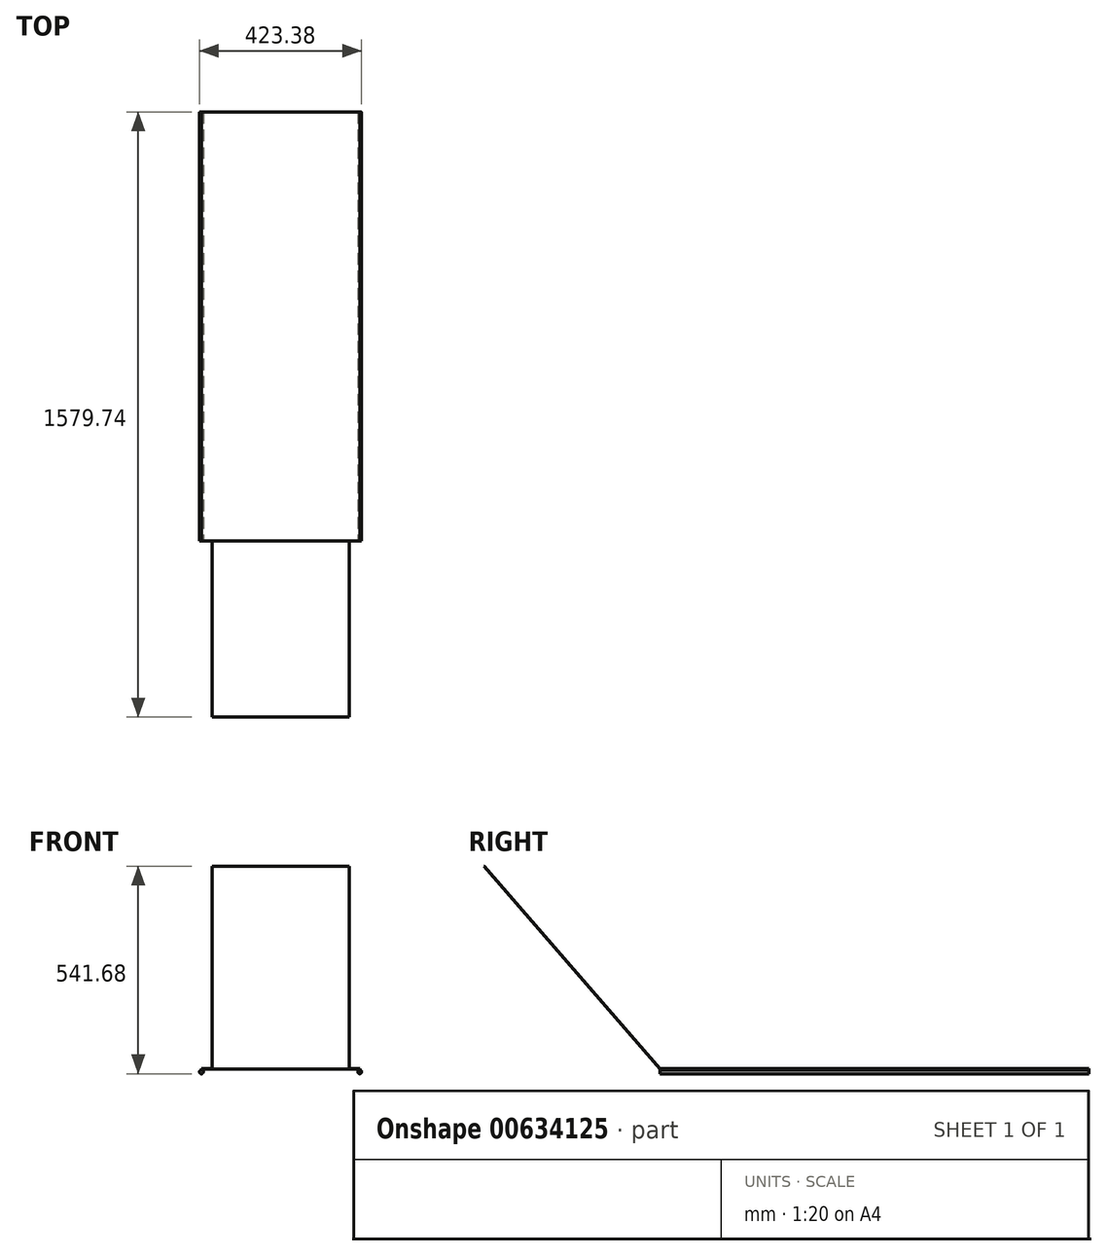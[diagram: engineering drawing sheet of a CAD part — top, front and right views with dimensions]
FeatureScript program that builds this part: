
annotation { "Feature Type Name" : "Feature", "Feature Type Description" : "" }
export const myFeature = defineFeature(function(context is Context, id is Id, definition is map)
    precondition{}
    {
        {
            var Q0;
            Q0=qCreatedBy(makeId("Front.planeOp"),FACE);
            var sketch = newSketch(context, id + "F0", { "sketchPlane" : qUnion([Q0])});
            skLineSegment(sketch, "E0.bottom", {"start": v(-15, 40) * mm, "end": v(15, 40) * mm});
            skLineSegment(sketch, "E0.top", {"start": v(-12, 0) * mm, "end": v(12, 0) * mm});
            skLineSegment(sketch, "E0.left", {"start": v(-15, 40) * mm, "end": v(-15, 37) * mm});
            skLineSegment(sketch, "E0.right", {"start": v(15, 37) * mm, "end": v(15, 3) * mm});
            skLineSegment(sketch, "E1.0", {"start": v(-15, 37) * mm, "end": v(3, 37) * mm});
            skLineSegment(sketch, "E1.1", {"start": v(-12, 6) * mm, "end": v(-12, 6) * mm});
            skLineSegment(sketch, "E1.2", {"start": v(-9, 3) * mm, "end": v(9, 3) * mm});
            skLineSegment(sketch, "E1.3", {"start": v(12, 29.6) * mm, "end": v(12, 6) * mm});
            skLineSegment(sketch, "E2.0", {"start": v(-15, 6) * mm, "end": v(-12, 6) * mm});
            skLineSegment(sketch, "E3", {"start": v(12, 40) * mm, "end": v(7.5, 40) * mm, "construction": true});
            skLineSegment(sketch, "E4", {"start": v(7, 34.8) * mm, "end": v(7, 40) * mm, "construction": true});
            skArc(sketch, "E5", {"start": v(7, 40) * mm, "mid": v(6.75, 29.6) * mm, "end": v(7.5, 39.98) * mm});
            skLineSegment(sketch, "E6.trimOffspring", {"start": v(-15, 6) * mm, "end": v(-15, 3) * mm});
            skPoint(sketch, "E7.orphan", {"position": v(5, 29.7) * mm});
            skPoint(sketch, "E8.visualSharp", {"position": v(15, 40) * mm});
            skArc(sketch, "E8.filletArc", {"start": v(15, 37) * mm, "mid": v(14.12, 39.12) * mm, "end": v(12, 40) * mm});
            skPoint(sketch, "E9.visualSharp", {"position": v(15, 0) * mm});
            skArc(sketch, "E9.filletArc", {"start": v(12, 0) * mm, "mid": v(14.12, 0.88) * mm, "end": v(15, 3) * mm});
            skArc(sketch, "E10.filletArc", {"start": v(9, 3) * mm, "mid": v(11.12, 3.88) * mm, "end": v(12, 6) * mm});
            skPoint(sketch, "E11.visualSharp", {"position": v(-12, 3) * mm});
            skArc(sketch, "E11.filletArc", {"start": v(-12, 6) * mm, "mid": v(-11.12, 3.88) * mm, "end": v(-9, 3) * mm});
            skPoint(sketch, "E12.visualSharp", {"position": v(-15, 0) * mm});
            skArc(sketch, "E12.filletArc", {"start": v(-15, 3) * mm, "mid": v(-14.12, 0.88) * mm, "end": v(-12, 0) * mm});
            skLineSegment(sketch, "E13.0", {"start": v(6.5, 34.8) * mm, "end": v(6.5, 39.8) * mm});
            skLineSegment(sketch, "E14.0", {"start": v(7.5, 34.8) * mm, "end": v(7.5, 40) * mm});
            skLineSegment(sketch, "E15", {"start": v(-15, 6) * mm, "end": v(-15, 16) * mm});
            skLineSegment(sketch, "E16", {"start": v(-15, 16) * mm, "end": v(-12, 16) * mm});
            skLineSegment(sketch, "E17", {"start": v(-12, 16) * mm, "end": v(-12, 6) * mm});
            skLineSegment(sketch, "E18", {"start": v(6.75, 29.6) * mm, "end": v(12, 29.6) * mm});
            skSolve(sketch);
        }
        {
            var Q0;
            Q0=qCreatedBy(makeId("Front.planeOp"),FACE);
            var sketch = newSketch(context, id + "F1", { "sketchPlane" : qUnion([Q0])});
            skLineSegment(sketch, "E19.1.1", {"start": v(7.5, 40) * mm, "end": v(-15, 40) * mm});
            skLineSegment(sketch, "E19.1.2", {"start": v(-15, 40) * mm, "end": v(-15, 37) * mm});
            skArc(sketch, "E19.2.8", {"start": v(-15, 3) * mm, "mid": v(-14.12, 0.88) * mm, "end": v(-12, 0) * mm, "construction": true});
            skLineSegment(sketch, "E19.2.9", {"start": v(-12, 0) * mm, "end": v(-5, 0) * mm});
            skLineSegment(sketch, "E19.2.13", {"start": v(17, 40) * mm, "end": v(8.5, 40) * mm});
            skLineSegment(sketch, "E19.3.0", {"start": v(-15, 18) * mm, "end": v(-15, 7.7) * mm});
            skPoint(sketch, "E20.2", {"position": v(6.5, 37.3) * mm});
            skPoint(sketch, "E21.orphan", {"position": v(6.5, 39.8) * mm});
            skPoint(sketch, "E19.0.2.end.orphan", {"position": v(7, 40) * mm});
            skPoint(sketch, "E22.orphan", {"position": v(12, 29.6) * mm});
            skPoint(sketch, "E23.orphan", {"position": v(7.5, 34.8) * mm});
            skPoint(sketch, "E20.0.start.orphan", {"position": v(6.5, 34.8) * mm});
            skLineSegment(sketch, "E24", {"start": v(-15, 37) * mm, "end": v(-15, 31) * mm});
            skLineSegment(sketch, "E25", {"start": v(0, 0) * mm, "end": v(0, 15) * mm, "construction": true});
            skLineSegment(sketch, "E26", {"start": v(7.5, 40) * mm, "end": v(7.5, 37.97) * mm});
            skLineSegment(sketch, "E27", {"start": v(8.5, 40) * mm, "end": v(8.5, 37.97) * mm});
            skLineSegment(sketch, "E28", {"start": v(15, 32.5) * mm, "end": v(8, 32.5) * mm, "construction": true});
            skPoint(sketch, "E29.orphan", {"position": v(7.6, 39) * mm});
            skLineSegment(sketch, "E30", {"start": v(8, 39) * mm, "end": v(8, 32.5) * mm, "construction": true});
            skPoint(sketch, "E19.3.3.end.orphan", {"position": v(-15, 16) * mm});
            skPoint(sketch, "E19.3.3.start.orphan", {"position": v(-12, 16) * mm});
            skLineSegment(sketch, "E31", {"start": v(-15, 3) * mm, "end": v(-15, 0) * mm});
            skLineSegment(sketch, "E32", {"start": v(-12, 0) * mm, "end": v(-15, 0) * mm});
            skLineSegment(sketch, "E33", {"start": v(-15, 40) * mm, "end": v(-15, 31) * mm, "construction": true});
            skLineSegment(sketch, "E34", {"start": v(-15, 40) * mm, "end": v(-15, 31) * mm});
            skLineSegment(sketch, "E35.trimOffspring", {"start": v(-15, 31) * mm, "end": v(-15, 26) * mm});
            skLineSegment(sketch, "E36.trimOffspring", {"start": v(-15, 29) * mm, "end": v(-15, 24) * mm});
            skPoint(sketch, "E37.orphan", {"position": v(12, 40) * mm});
            skPoint(sketch, "E38.orphan", {"position": v(12, 0) * mm});
            skLineSegment(sketch, "E39.0", {"start": v(13.1, 38) * mm, "end": v(13.1, 38) * mm});
            skLineSegment(sketch, "E40.1", {"start": v(-13, 2) * mm, "end": v(-11, 2) * mm, "construction": true});
            skLineSegment(sketch, "E41.0", {"start": v(-13, 38) * mm, "end": v(-13, 34) * mm});
            skArc(sketch, "E42", {"start": v(13.32, 33.87) * mm, "mid": v(11.56, 36.69) * mm, "end": v(8.5, 37.97) * mm});
            skLineSegment(sketch, "E43.0", {"start": v(29.42, 20) * mm, "end": v(-7, 20) * mm, "construction": true});
            skLineSegment(sketch, "E44.trimOffspring", {"start": v(-13, 0.17) * mm, "end": v(-13, 0) * mm});
            skArc(sketch, "E45.0", {"start": v(2.9, 38) * mm, "mid": v(3.81, 26.3) * mm, "end": v(15, 29.84) * mm});
            skLineSegment(sketch, "E46.trimOffspring", {"start": v(2.9, 38) * mm, "end": v(-13, 38) * mm});
            skLineSegment(sketch, "E47.trimOffspring", {"start": v(13.32, 33.87) * mm, "end": v(13.43, 31.7) * mm});
            skArc(sketch, "E48.trimOffspring", {"start": v(13.1, 38) * mm, "mid": v(13.1, 38) * mm, "end": v(13.1, 38) * mm});
            skArc(sketch, "E49.trimOffspring", {"start": v(7.5, 37.97) * mm, "mid": v(4.01, 28.73) * mm, "end": v(13.43, 31.7) * mm});
            skPoint(sketch, "E50.orphan", {"position": v(7.5, 39) * mm});
            skPoint(sketch, "E51.start.orphan", {"position": v(8.5, 39) * mm});
            skLineSegment(sketch, "E52.0", {"start": v(8, 0) * mm, "end": v(8, 13.5) * mm});
            skLineSegment(sketch, "E53.0", {"start": v(-5, 0) * mm, "end": v(-5, 13.5) * mm});
            skLineSegment(sketch, "E54.0", {"start": v(16.47, 12) * mm, "end": v(14.46, 12) * mm, "construction": true});
            skLineSegment(sketch, "E55.trimOffspring", {"start": v(12.84, 12) * mm, "end": v(10, 12) * mm});
            skLineSegment(sketch, "E56.0", {"start": v(1.5, 0) * mm, "end": v(1.5, 20) * mm, "construction": true});
            skLineSegment(sketch, "E57", {"start": v(1.5, 20) * mm, "end": v(-9.16, 15.5) * mm});
            skLineSegment(sketch, "E58", {"start": v(1.5, 20) * mm, "end": v(10.84, 15.5) * mm});
            skLineSegment(sketch, "E59.0", {"start": v(-9.16, 13.5) * mm, "end": v(-5, 13.5) * mm});
            skLineSegment(sketch, "E60", {"start": v(-9.16, 15.5) * mm, "end": v(-9.16, 13.5) * mm});
            skLineSegment(sketch, "E61", {"start": v(10.84, 15.5) * mm, "end": v(10.84, 13.5) * mm});
            skLineSegment(sketch, "E62.trimOffspring", {"start": v(8, 13.5) * mm, "end": v(10.84, 13.5) * mm});
            skLineSegment(sketch, "E63.trimOffspring", {"start": v(10, 2) * mm, "end": v(15, 2) * mm});
            skLineSegment(sketch, "E64.trimOffspring", {"start": v(8, 0) * mm, "end": v(17, 0) * mm});
            skLineSegment(sketch, "E65.0", {"start": v(10, 2) * mm, "end": v(10, 12) * mm});
            skLineSegment(sketch, "E66.0", {"start": v(1.55, 22.2) * mm, "end": v(-7, 18.58) * mm});
            skLineSegment(sketch, "E66.1", {"start": v(1.55, 22.2) * mm, "end": v(12.84, 16.75) * mm});
            skLineSegment(sketch, "E67.0", {"start": v(-11.16, 16.82) * mm, "end": v(-11.16, 15.5) * mm});
            skLineSegment(sketch, "E68.0", {"start": v(-13, 11.5) * mm, "end": v(-7, 11.5) * mm});
            skLineSegment(sketch, "E69", {"start": v(-11.16, 15.5) * mm, "end": v(-11.16, 13.5) * mm});
            skLineSegment(sketch, "E70.0", {"start": v(12.84, 16.75) * mm, "end": v(12.84, 12) * mm});
            skLineSegment(sketch, "E71.0", {"start": v(-13, 6.7) * mm, "end": v(-7, 6.7) * mm, "construction": true});
            skLineSegment(sketch, "E72.0", {"start": v(-15, 7.7) * mm, "end": v(-13, 7.7) * mm});
            skLineSegment(sketch, "E73.0", {"start": v(-15, 5.7) * mm, "end": v(-11, 5.7) * mm});
            skLineSegment(sketch, "E74.0", {"start": v(-15, 3.7) * mm, "end": v(-13, 3.7) * mm, "construction": true});
            skLineSegment(sketch, "E75.trimOffspring", {"start": v(-15, 5.7) * mm, "end": v(-15, 3) * mm});
            skLineSegment(sketch, "E76.trimOffspring", {"start": v(-13, 3.7) * mm, "end": v(-13, 2) * mm, "construction": true});
            skLineSegment(sketch, "E77.trimOffspring", {"start": v(-11, 5.7) * mm, "end": v(-11, 2) * mm});
            skLineSegment(sketch, "E78.0", {"start": v(-13, 13.5) * mm, "end": v(-11.16, 13.5) * mm});
            skLineSegment(sketch, "E79.trimOffspring", {"start": v(-9.16, 13.5) * mm, "end": v(-7, 13.5) * mm});
            skLineSegment(sketch, "E80.trimOffspring", {"start": v(-13, 11.5) * mm, "end": v(-13, 7.7) * mm});
            skLineSegment(sketch, "E81.0", {"start": v(-7, 11.5) * mm, "end": v(-7, 3.7) * mm});
            skLineSegment(sketch, "E82.trimOffspring", {"start": v(-11, 3.7) * mm, "end": v(-7, 3.7) * mm});
            skLineSegment(sketch, "E83.0", {"start": v(17, 40) * mm, "end": v(17, 0) * mm});
            skPoint(sketch, "E84.orphan", {"position": v(17.1, 0) * mm});
            skLineSegment(sketch, "E85.trimOffspring", {"start": v(15, 29.84) * mm, "end": v(15, 2) * mm});
            skPoint(sketch, "E86.start.orphan", {"position": v(15, 40) * mm});
            skLineSegment(sketch, "E87", {"start": v(-13, 13.5) * mm, "end": v(-13, 18) * mm});
            skLineSegment(sketch, "E88.trimOffspring", {"start": v(-15, 22) * mm, "end": v(-15, 21.16) * mm, "construction": true});
            skLineSegment(sketch, "E89.trimOffspring", {"start": v(-15, 22) * mm, "end": v(-15, 18) * mm});
            skPoint(sketch, "E90.start.orphan", {"position": v(-12, 28) * mm});
            skPoint(sketch, "E91.orphan", {"position": v(-12, 29) * mm});
            skLineSegment(sketch, "E92.0", {"start": v(-9, 26) * mm, "end": v(-11, 26) * mm});
            skLineSegment(sketch, "E93.0", {"start": v(-11, 24) * mm, "end": v(-13, 24) * mm});
            skLineSegment(sketch, "E94", {"start": v(-9, 20) * mm, "end": v(-9, 26) * mm});
            skLineSegment(sketch, "E95.0", {"start": v(-11, 20) * mm, "end": v(-11, 22) * mm});
            skLineSegment(sketch, "E96.trimOffspring", {"start": v(-11, 24) * mm, "end": v(-11, 26) * mm});
            skLineSegment(sketch, "E97.trimOffspring", {"start": v(-13, 28) * mm, "end": v(-13, 34) * mm});
            skLineSegment(sketch, "E98", {"start": v(-15, 22) * mm, "end": v(-11, 22) * mm});
            skLineSegment(sketch, "E99", {"start": v(-13, 24) * mm, "end": v(-15, 24) * mm});
            skLineSegment(sketch, "E100.0", {"start": v(-7, 18.58) * mm, "end": v(-7, 28) * mm});
            skLineSegment(sketch, "E101.0", {"start": v(-13, 18) * mm, "end": v(-8.36, 18) * mm});
            skLineSegment(sketch, "E102.trimOffspring", {"start": v(-8.36, 18) * mm, "end": v(-11.16, 16.82) * mm});
            skLineSegment(sketch, "E103.0", {"start": v(-11, 20) * mm, "end": v(-9, 20) * mm});
            skLineSegment(sketch, "E104.0", {"start": v(-7, 28) * mm, "end": v(-13, 28) * mm});
            skSolve(sketch);
        }
        {
            var Q0;
            Q0=qSketchRegion(id+"F1",true);
            extrude(context, id + "F2", {"entities" : qUnion([Q0]), "oppositeDirection" : true, "depth" : 1910 * mm, "offsetDistance" : 25 * mm});
        }
        {
            var Q0;
            Q0=makeQuery(id+"F1.imprint","IMPRINT",FACE,{"disambiguationData":[TD([[makeQuery(id+"F1.imprint","IMPRINT",EDGE,{"derivedFrom":sQuery(id+"F1.wireOp",EDGE,"E19.1.1")}),1.0]])]});
            var sketch = newSketch(context, id + "F3", { "sketchPlane" : qUnion([Q0])});
            skLineSegment(sketch, "E105.0", {"start": v(-13.5, 18) * mm, "end": v(-13.5, -0.51) * mm});
            skSolve(sketch);
        }
        {
            var Q0;
            Q0=makeQuery(id+"F3.imprint","IMPRINT",FACE,{"disambiguationData":[TD([[makeQuery(id+"F3.imprint","IMPRINT",EDGE,{"derivedFrom":makeQuery(id+"F1.imprint","IMPRINT",EDGE,{"derivedFrom":sQuery(id+"F1.wireOp",EDGE,"E19.1.1")})}),1.0]])]});
            var sketch = newSketch(context, id + "F4", { "sketchPlane" : qUnion([Q0])});
            skLineSegment(sketch, "E106.0", {"start": v(-17, 40) * mm, "end": v(-25.5, 40) * mm});
            skLineSegment(sketch, "E107.0", {"start": v(-49.1, 40) * mm, "end": v(-49.1, 18) * mm});
            skLineSegment(sketch, "E108.0", {"start": v(-17, 40) * mm, "end": v(-17, 18) * mm});
            skPoint(sketch, "E109.orphan", {"position": v(7.5, 40) * mm});
            skLineSegment(sketch, "E110.1", {"start": v(-19, 29.83) * mm, "end": v(-19, 20) * mm});
            skLineSegment(sketch, "E110.3", {"start": v(-47.1, 38) * mm, "end": v(-47.1, 20) * mm});
            skArc(sketch, "E111.0", {"start": v(7.5, 37.97) * mm, "mid": v(4.01, 28.73) * mm, "end": v(13.43, 31.7) * mm, "construction": true});
            skLineSegment(sketch, "E112.0", {"start": v(17, 40) * mm, "end": v(8.5, 40) * mm});
            skLineSegment(sketch, "E113.0", {"start": v(7.5, 40) * mm, "end": v(-15, 40) * mm});
            skLineSegment(sketch, "E114.0", {"start": v(-26.6, 40) * mm, "end": v(-26.6, 37.97) * mm});
            skLineSegment(sketch, "E115.0", {"start": v(-25.5, 40) * mm, "end": v(-25.5, 37.98) * mm});
            skLineSegment(sketch, "E116.0", {"start": v(-7, 18.58) * mm, "end": v(-7, 28) * mm});
            skLineSegment(sketch, "E117", {"start": v(-47.1, 23.29) * mm, "end": v(15, 23.29) * mm, "construction": true});
            skPoint(sketch, "E118.orphan", {"position": v(-7, 23.29) * mm});
            skLineSegment(sketch, "E119", {"start": v(8, 32.5) * mm, "end": v(2.5, 32.5) * mm});
            skLineSegment(sketch, "E120.0", {"start": v(8, 39) * mm, "end": v(8, 32.5) * mm});
            skLineSegment(sketch, "E120.1", {"start": v(17, 40) * mm, "end": v(17, 0) * mm});
            skLineSegment(sketch, "E121.trimOffspring", {"start": v(-17, 32.5) * mm, "end": v(-26, 32.5) * mm, "construction": true});
            skArc(sketch, "E122", {"start": v(-26.6, 37.97) * mm, "mid": v(-25.95, 27.01) * mm, "end": v(-25.5, 37.98) * mm});
            skArc(sketch, "E123.0", {"start": v(-31.1, 38) * mm, "mid": v(-30.2, 26.3) * mm, "end": v(-19, 29.83) * mm});
            skLineSegment(sketch, "E124.trimOffspring", {"start": v(-26.6, 40) * mm, "end": v(-49.1, 40) * mm});
            skLineSegment(sketch, "E125.trimOffspring", {"start": v(-26.6, 27.05) * mm, "end": v(-26.6, 20) * mm, "construction": true});
            skLineSegment(sketch, "E126.trimOffspring", {"start": v(-25.5, 27.04) * mm, "end": v(-25.5, 20) * mm, "construction": true});
            skLineSegment(sketch, "E127.trimOffspring", {"start": v(-31.1, 38) * mm, "end": v(-47.1, 38) * mm});
            skLineSegment(sketch, "E128.0", {"start": v(-49.1, 18) * mm, "end": v(-17, 18) * mm});
            skPoint(sketch, "E129.orphan", {"position": v(-8.36, 18) * mm});
            skPoint(sketch, "E130.orphan", {"position": v(-13, 18) * mm});
            skLineSegment(sketch, "E131.0", {"start": v(-47.1, 20) * mm, "end": v(-19, 20) * mm});
            skSolve(sketch);
        }
        {
            var Q0;
            Q0=makeQuery(id+"F1.imprint","IMPRINT",FACE,{"disambiguationData":[TD([[makeQuery(id+"F1.imprint","IMPRINT",EDGE,{"derivedFrom":sQuery(id+"F1.wireOp",EDGE,"E19.1.1")}),1.0]])]});
            var sketch = newSketch(context, id + "F5", { "sketchPlane" : qUnion([Q0])});
            skArc(sketch, "E132.0", {"start": v(7.5, 37.97) * mm, "mid": v(4.01, 28.73) * mm, "end": v(13.43, 31.7) * mm, "construction": true});
            skArc(sketch, "E132.1", {"start": v(13.32, 33.87) * mm, "mid": v(11.56, 36.69) * mm, "end": v(8.5, 37.97) * mm, "construction": true});
            skLineSegment(sketch, "E132.2", {"start": v(7.5, 40) * mm, "end": v(-15, 40) * mm});
            skArc(sketch, "E132.3", {"start": v(-26.6, 37.97) * mm, "mid": v(-25.95, 27.01) * mm, "end": v(-25.5, 37.98) * mm, "construction": true});
            skLineSegment(sketch, "E133.0", {"start": v(-15, 40) * mm, "end": v(-25.5, 40) * mm});
            skPoint(sketch, "E134.orphan", {"position": v(-26.6, 40) * mm});
            skLineSegment(sketch, "E135.0", {"start": v(7.5, 40) * mm, "end": v(7.5, 37.37) * mm});
            skLineSegment(sketch, "E135.1", {"start": v(8.5, 40) * mm, "end": v(8.5, 37.37) * mm});
            skLineSegment(sketch, "E135.2", {"start": v(-25.5, 40) * mm, "end": v(-25.5, 37.37) * mm});
            skLineSegment(sketch, "E135.3", {"start": v(-26.6, 40) * mm, "end": v(-26.6, 37.36) * mm});
            skPoint(sketch, "E135.4", {"position": v(-25.5, 38.99) * mm});
            skLineSegment(sketch, "E136", {"start": v(-49.1, 40) * mm, "end": v(-198.8, 40) * mm});
            skLineSegment(sketch, "E137.0", {"start": v(8.5, 41) * mm, "end": v(-198.8, 41) * mm});
            skLineSegment(sketch, "E138", {"start": v(8.5, 40) * mm, "end": v(8.5, 41) * mm});
            skLineSegment(sketch, "E139", {"start": v(-198.8, 41) * mm, "end": v(-198.8, 40) * mm, "construction": true});
            skArc(sketch, "E140.0", {"start": v(7.5, 37.37) * mm, "mid": v(4.47, 29.12) * mm, "end": v(12.84, 31.8) * mm});
            skArc(sketch, "E141.0", {"start": v(12.74, 33.72) * mm, "mid": v(11.2, 36.21) * mm, "end": v(8.5, 37.37) * mm});
            skArc(sketch, "E142", {"start": v(12.74, 33.72) * mm, "mid": v(12.88, 32.76) * mm, "end": v(12.84, 31.8) * mm});
            skPoint(sketch, "E143.orphan", {"position": v(7.5, 37.97) * mm});
            skPoint(sketch, "E144.orphan", {"position": v(8.5, 37.97) * mm});
            skArc(sketch, "E145.0", {"start": v(-26.6, 37.36) * mm, "mid": v(-25.95, 27.61) * mm, "end": v(-25.5, 37.37) * mm});
            skPoint(sketch, "E146.orphan", {"position": v(-26.6, 37.97) * mm});
            skPoint(sketch, "E147.orphan", {"position": v(-25.5, 37.98) * mm});
            skLineSegment(sketch, "E148.trimOffspring", {"start": v(-26.6, 40) * mm, "end": v(-49.1, 40) * mm});
            skSolve(sketch);
        }
        {
            var Q0;
            Q0=qCreatedBy(makeId("Front.planeOp"),FACE);
            var sketch = newSketch(context, id + "F6", { "sketchPlane" : qUnion([Q0])});
            skLineSegment(sketch, "E149.3", {"start": v(8.5, 40) * mm, "end": v(8.5, 37.37) * mm});
            skLineSegment(sketch, "E149.4", {"start": v(7.5, 40) * mm, "end": v(7.5, 37.37) * mm});
            skLineSegment(sketch, "E149.5", {"start": v(7.5, 40) * mm, "end": v(-15, 40) * mm});
            skLineSegment(sketch, "E149.6", {"start": v(8.5, 41) * mm, "end": v(-198.8, 41) * mm});
            skLineSegment(sketch, "E149.7", {"start": v(8.5, 40) * mm, "end": v(8.5, 41) * mm});
            skLineSegment(sketch, "E149.8", {"start": v(-25.5, 40) * mm, "end": v(-198.8, 40) * mm});
            skLineSegment(sketch, "E149.9", {"start": v(-198.8, 41) * mm, "end": v(-198.8, 40) * mm});
            skLineSegment(sketch, "E150.0", {"start": v(-15, 40) * mm, "end": v(-25.5, 40) * mm});
            skLineSegment(sketch, "E151.0", {"start": v(8, 32.5) * mm, "end": v(2.5, 32.5) * mm, "construction": true});
            skLineSegment(sketch, "E151.1", {"start": v(8, 39) * mm, "end": v(8, 32.5) * mm, "construction": true});
            skArc(sketch, "E152", {"start": v(7.5, 37.37) * mm, "mid": v(8, 27.62) * mm, "end": v(8.5, 37.37) * mm});
            skPoint(sketch, "E153.orphan", {"position": v(-49.1, 40) * mm});
            skSolve(sketch);
        }
        {
            var Q0;
            Q0=qSketchRegion(id+"F6",true);
            extrude(context, id + "F7", {"entities" : qUnion([Q0]), "operationType" : NewBodyOperationType.ADD, "oppositeDirection" : true, "depth" : 1120 * mm, "offsetDistance" : 25 * mm});
        }
        {
            var Q0;
            {var subQ7=sQuery(id+"F5.wireOp",EDGE,"E132.2");Q0=makeQuery(id+"F5.imprint","IMPRINT",FACE,{"disambiguationData":[TD([[makeQuery(id+"F5.imprint","IMPRINT",EDGE,{"derivedFrom":subQ7}),1.0]])]});}
            var sketch = newSketch(context, id + "F8", { "sketchPlane" : qUnion([Q0])});
            skLineSegment(sketch, "E154.0.0", {"start": v(-15, 0) * mm, "end": v(-13, 0) * mm});
            skLineSegment(sketch, "E154.0.1", {"start": v(-13, 0) * mm, "end": v(-12, 0) * mm});
            skLineSegment(sketch, "E154.0.2", {"start": v(-12, 0) * mm, "end": v(-5, 0) * mm});
            skLineSegment(sketch, "E154.0.3", {"start": v(-5, 0) * mm, "end": v(-5, 13.5) * mm});
            skLineSegment(sketch, "E154.0.4", {"start": v(-5, 13.5) * mm, "end": v(-7, 13.5) * mm});
            skLineSegment(sketch, "E154.0.5", {"start": v(-7, 13.5) * mm, "end": v(-9.16, 13.5) * mm});
            skLineSegment(sketch, "E154.0.6", {"start": v(-9.16, 13.5) * mm, "end": v(-9.16, 15.5) * mm});
            skLineSegment(sketch, "E154.0.7", {"start": v(-9.16, 15.5) * mm, "end": v(1.5, 20) * mm});
            skLineSegment(sketch, "E154.0.8", {"start": v(1.5, 20) * mm, "end": v(10.84, 15.5) * mm});
            skLineSegment(sketch, "E154.0.9", {"start": v(10.84, 15.5) * mm, "end": v(10.84, 13.5) * mm});
            skLineSegment(sketch, "E154.0.10", {"start": v(10.84, 13.5) * mm, "end": v(8, 13.5) * mm});
            skLineSegment(sketch, "E154.0.11", {"start": v(8, 13.5) * mm, "end": v(8, 0) * mm});
            skLineSegment(sketch, "E154.0.12", {"start": v(8, 0) * mm, "end": v(17, 0) * mm});
            skLineSegment(sketch, "E154.0.13", {"start": v(17, 0) * mm, "end": v(17, 40) * mm});
            skLineSegment(sketch, "E154.0.14", {"start": v(17, 40) * mm, "end": v(8.5, 40) * mm});
            skLineSegment(sketch, "E154.0.15", {"start": v(8.5, 40) * mm, "end": v(8.5, 37.97) * mm});
            skArc(sketch, "E154.0.16", {"start": v(8.5, 37.97) * mm, "mid": v(11.56, 36.69) * mm, "end": v(13.32, 33.87) * mm});
            skLineSegment(sketch, "E154.0.17", {"start": v(13.32, 33.87) * mm, "end": v(13.43, 31.7) * mm});
            skArc(sketch, "E154.0.18", {"start": v(13.43, 31.7) * mm, "mid": v(4.01, 28.73) * mm, "end": v(7.5, 37.97) * mm});
            skLineSegment(sketch, "E154.0.19", {"start": v(7.5, 37.97) * mm, "end": v(7.5, 40) * mm});
            skLineSegment(sketch, "E154.0.20", {"start": v(7.5, 40) * mm, "end": v(-15, 40) * mm});
            skLineSegment(sketch, "E154.0.21", {"start": v(-15, 40) * mm, "end": v(-15, 31) * mm});
            skLineSegment(sketch, "E154.0.22", {"start": v(-15, 31) * mm, "end": v(-15, 29) * mm});
            skLineSegment(sketch, "E154.0.23", {"start": v(-15, 29) * mm, "end": v(-15, 24) * mm});
            skLineSegment(sketch, "E154.0.24", {"start": v(-15, 24) * mm, "end": v(-13, 24) * mm});
            skLineSegment(sketch, "E154.0.25", {"start": v(-13, 24) * mm, "end": v(-11, 24) * mm});
            skLineSegment(sketch, "E154.0.26", {"start": v(-11, 24) * mm, "end": v(-11, 26) * mm});
            skLineSegment(sketch, "E154.0.27", {"start": v(-11, 26) * mm, "end": v(-9, 26) * mm});
            skLineSegment(sketch, "E154.0.28", {"start": v(-9, 26) * mm, "end": v(-9, 20) * mm});
            skLineSegment(sketch, "E154.0.29", {"start": v(-9, 20) * mm, "end": v(-11, 20) * mm});
            skLineSegment(sketch, "E154.0.30", {"start": v(-11, 20) * mm, "end": v(-11, 22) * mm});
            skLineSegment(sketch, "E154.0.31", {"start": v(-11, 22) * mm, "end": v(-15, 22) * mm});
            skLineSegment(sketch, "E154.0.32", {"start": v(-15, 22) * mm, "end": v(-15, 18) * mm});
            skLineSegment(sketch, "E154.0.33", {"start": v(-15, 18) * mm, "end": v(-15, 7.7) * mm});
            skLineSegment(sketch, "E154.0.34", {"start": v(-15, 7.7) * mm, "end": v(-13, 7.7) * mm});
            skLineSegment(sketch, "E154.0.35", {"start": v(-13, 7.7) * mm, "end": v(-13, 11.5) * mm});
            skLineSegment(sketch, "E154.0.36", {"start": v(-13, 11.5) * mm, "end": v(-7, 11.5) * mm});
            skLineSegment(sketch, "E154.0.37", {"start": v(-7, 11.5) * mm, "end": v(-7, 3.7) * mm});
            skLineSegment(sketch, "E154.0.38", {"start": v(-7, 3.7) * mm, "end": v(-11, 3.7) * mm});
            skLineSegment(sketch, "E154.0.39", {"start": v(-11, 3.7) * mm, "end": v(-11, 5.7) * mm});
            skLineSegment(sketch, "E154.0.40", {"start": v(-11, 5.7) * mm, "end": v(-15, 5.7) * mm});
            skLineSegment(sketch, "E154.0.41", {"start": v(-15, 5.7) * mm, "end": v(-15, 3) * mm});
            skLineSegment(sketch, "E154.0.42", {"start": v(-15, 3) * mm, "end": v(-15, 0) * mm});
            skLineSegment(sketch, "E155.0.0", {"start": v(12.84, 16.75) * mm, "end": v(12.84, 12) * mm});
            skLineSegment(sketch, "E155.0.1", {"start": v(12.84, 12) * mm, "end": v(10, 12) * mm});
            skLineSegment(sketch, "E155.0.2", {"start": v(10, 12) * mm, "end": v(10, 2) * mm});
            skLineSegment(sketch, "E155.0.3", {"start": v(10, 2) * mm, "end": v(15, 2) * mm});
            skLineSegment(sketch, "E155.0.4", {"start": v(15, 2) * mm, "end": v(15, 29.84) * mm});
            skArc(sketch, "E155.0.5", {"start": v(15, 29.84) * mm, "mid": v(3.81, 26.3) * mm, "end": v(2.9, 38) * mm});
            skLineSegment(sketch, "E155.0.6", {"start": v(2.9, 38) * mm, "end": v(-13, 38) * mm});
            skLineSegment(sketch, "E155.0.7", {"start": v(-13, 38) * mm, "end": v(-13, 34) * mm});
            skLineSegment(sketch, "E155.0.8", {"start": v(-13, 34) * mm, "end": v(-13, 28) * mm});
            skLineSegment(sketch, "E155.0.9", {"start": v(-13, 28) * mm, "end": v(-7, 28) * mm});
            skLineSegment(sketch, "E155.0.10", {"start": v(-7, 28) * mm, "end": v(-7, 18.58) * mm});
            skLineSegment(sketch, "E155.0.11", {"start": v(-7, 18.58) * mm, "end": v(1.55, 22.2) * mm});
            skLineSegment(sketch, "E155.0.12", {"start": v(1.55, 22.2) * mm, "end": v(12.84, 16.75) * mm});
            skLineSegment(sketch, "E156.0.0", {"start": v(-8.36, 18) * mm, "end": v(-13, 18) * mm});
            skLineSegment(sketch, "E156.0.1", {"start": v(-13, 18) * mm, "end": v(-13, 13.5) * mm});
            skLineSegment(sketch, "E156.0.2", {"start": v(-13, 13.5) * mm, "end": v(-11.16, 13.5) * mm});
            skLineSegment(sketch, "E156.0.3", {"start": v(-11.16, 13.5) * mm, "end": v(-11.16, 15.5) * mm});
            skLineSegment(sketch, "E156.0.4", {"start": v(-11.16, 15.5) * mm, "end": v(-11.16, 16.82) * mm});
            skLineSegment(sketch, "E156.0.5", {"start": v(-11.16, 16.82) * mm, "end": v(-8.36, 18) * mm});
            skSolve(sketch);
        }
        {
            var Q0;
            Q0=qSketchRegion(id+"F8",true);
            extrude(context, id + "F9", {"entities" : qUnion([Q0]), "operationType" : NewBodyOperationType.REMOVE, "oppositeDirection" : true, "depth" : 2000 * mm, "offsetDistance" : 25 * mm});
        }
        {
            var Q0;
            Q0=makeQuery(id+"F7.boolean.opBoolean","MERGE",FACE,{"derivedFrom":[makeQuery(id+"F2.opExtrude","CAP_FACE",FACE,{"disambiguationData":[OSD([sQuery(id+"F1.wireOp",EDGE,"E19.1.1"),sQuery(id+"F1.wireOp",EDGE,"E19.2.9"),sQuery(id+"F1.wireOp",EDGE,"E19.2.13"),sQuery(id+"F1.wireOp",EDGE,"E19.3.0"),sQuery(id+"F1.wireOp",EDGE,"E26"),sQuery(id+"F1.wireOp",EDGE,"E27"),sQuery(id+"F1.wireOp",EDGE,"E31"),sQuery(id+"F1.wireOp",EDGE,"E32"),sQuery(id+"F1.wireOp",EDGE,"E34"),sQuery(id+"F1.wireOp",EDGE,"E35.trimOffspring"),sQuery(id+"F1.wireOp",EDGE,"E36.trimOffspring"),sQuery(id+"F1.wireOp",EDGE,"E39.0"),sQuery(id+"F1.wireOp",EDGE,"E39.0"),sQuery(id+"F1.wireOp",EDGE,"E41.0"),sQuery(id+"F1.wireOp",EDGE,"E42"),sQuery(id+"F1.wireOp",EDGE,"E45.0"),sQuery(id+"F1.wireOp",EDGE,"E46.trimOffspring"),sQuery(id+"F1.wireOp",EDGE,"E47.trimOffspring"),sQuery(id+"F1.wireOp",EDGE,"E48.trimOffspring"),sQuery(id+"F1.wireOp",EDGE,"E49.trimOffspring"),sQuery(id+"F1.wireOp",EDGE,"E52.0"),sQuery(id+"F1.wireOp",EDGE,"E53.0"),sQuery(id+"F1.wireOp",EDGE,"E55.trimOffspring"),sQuery(id+"F1.wireOp",EDGE,"E57"),sQuery(id+"F1.wireOp",EDGE,"E58"),sQuery(id+"F1.wireOp",EDGE,"E59.0"),sQuery(id+"F1.wireOp",EDGE,"E60"),sQuery(id+"F1.wireOp",EDGE,"E61"),sQuery(id+"F1.wireOp",EDGE,"E62.trimOffspring"),sQuery(id+"F1.wireOp",EDGE,"E63.trimOffspring"),sQuery(id+"F1.wireOp",EDGE,"E64.trimOffspring"),sQuery(id+"F1.wireOp",EDGE,"E65.0"),sQuery(id+"F1.wireOp",EDGE,"E66.0"),sQuery(id+"F1.wireOp",EDGE,"E66.1"),sQuery(id+"F1.wireOp",EDGE,"E67.0"),sQuery(id+"F1.wireOp",EDGE,"E68.0"),sQuery(id+"F1.wireOp",EDGE,"E69"),sQuery(id+"F1.wireOp",EDGE,"E70.0"),sQuery(id+"F1.wireOp",EDGE,"E72.0"),sQuery(id+"F1.wireOp",EDGE,"E73.0"),sQuery(id+"F1.wireOp",EDGE,"E75.trimOffspring"),sQuery(id+"F1.wireOp",EDGE,"E77.trimOffspring"),sQuery(id+"F1.wireOp",EDGE,"E78.0"),sQuery(id+"F1.wireOp",EDGE,"E79.trimOffspring"),sQuery(id+"F1.wireOp",EDGE,"E80.trimOffspring"),sQuery(id+"F1.wireOp",EDGE,"E81.0"),sQuery(id+"F1.wireOp",EDGE,"E82.trimOffspring"),sQuery(id+"F1.wireOp",EDGE,"E83.0"),sQuery(id+"F1.wireOp",EDGE,"E85.trimOffspring"),sQuery(id+"F1.wireOp",EDGE,"E87"),sQuery(id+"F1.wireOp",EDGE,"E89.trimOffspring"),sQuery(id+"F1.wireOp",EDGE,"E92.0"),sQuery(id+"F1.wireOp",EDGE,"E93.0"),sQuery(id+"F1.wireOp",EDGE,"E94"),sQuery(id+"F1.wireOp",EDGE,"E95.0"),sQuery(id+"F1.wireOp",EDGE,"E96.trimOffspring"),sQuery(id+"F1.wireOp",EDGE,"E97.trimOffspring"),sQuery(id+"F1.wireOp",EDGE,"E98"),sQuery(id+"F1.wireOp",EDGE,"E99"),sQuery(id+"F1.wireOp",EDGE,"E100.0"),sQuery(id+"F1.wireOp",EDGE,"E101.0"),sQuery(id+"F1.wireOp",EDGE,"E102.trimOffspring"),sQuery(id+"F1.wireOp",EDGE,"E103.0"),sQuery(id+"F1.wireOp",EDGE,"E104.0")])],"isStart":true}),makeQuery(id+"F7.opExtrude","CAP_FACE",FACE,{"disambiguationData":[OSD([sQuery(id+"F6.wireOp",EDGE,"E149.3"),sQuery(id+"F6.wireOp",EDGE,"E149.4"),sQuery(id+"F6.wireOp",EDGE,"E149.5"),sQuery(id+"F6.wireOp",EDGE,"E149.6"),sQuery(id+"F6.wireOp",EDGE,"E149.7"),sQuery(id+"F6.wireOp",EDGE,"E149.8"),sQuery(id+"F6.wireOp",EDGE,"E149.9"),sQuery(id+"F6.wireOp",EDGE,"E150.0"),sQuery(id+"F6.wireOp",EDGE,"E152")])],"isStart":true})]});
            var sketch = newSketch(context, id + "F10", { "sketchPlane" : qUnion([Q0])});
            skLineSegment(sketch, "E157.0", {"start": v(-26.6, 40) * mm, "end": v(-26.6, 37.97) * mm});
            skLineSegment(sketch, "E157.1", {"start": v(-25.5, 41) * mm, "end": v(-25.5, 37.98) * mm});
            skArc(sketch, "E157.2", {"start": v(-26.6, 37.97) * mm, "mid": v(-25.95, 27.01) * mm, "end": v(-25.5, 37.98) * mm});
            skLineSegment(sketch, "E157.3", {"start": v(-25.5, 41) * mm, "end": v(-198.8, 41) * mm});
            skLineSegment(sketch, "E157.4", {"start": v(-26.6, 40) * mm, "end": v(-49.1, 40) * mm});
            skPoint(sketch, "E158.orphan", {"position": v(-25.5, 40) * mm});
            skPoint(sketch, "E159.orphan", {"position": v(8.5, 41) * mm});
            skLineSegment(sketch, "E160.0", {"start": v(-26.6, 40) * mm, "end": v(-198.8, 40) * mm});
            skPoint(sketch, "E161.orphan", {"position": v(7.5, 40) * mm});
            skLineSegment(sketch, "E162.0", {"start": v(-198.8, 41) * mm, "end": v(-198.8, 40) * mm});
            skSolve(sketch);
        }
        {
            var Q0;
            Q0=makeQuery(id+"F7.opExtrude","SWEPT_FACE",FACE,{"disambiguationData":[OSD([sQuery(id+"F6.wireOp",EDGE,"E149.9")])]});
            var sketch = newSketch(context, id + "F11", { "sketchPlane" : qUnion([Q0])});
            skLineSegment(sketch, "E163", {"start": v(0, 41) * mm, "end": v(459.24, 569.3) * mm});
            skLineSegment(sketch, "E164.0", {"start": v(0, 41) * mm, "end": v(0, 40) * mm});
            skPoint(sketch, "E165.orphan", {"position": v(0, 38) * mm});
            skPoint(sketch, "E166.orphan", {"position": v(0, 20) * mm});
            skLineSegment(sketch, "E167", {"start": v(0, 40) * mm, "end": v(459.74, 568.87) * mm});
            skLineSegment(sketch, "E168", {"start": v(459.24, 569.3) * mm, "end": v(459.74, 568.87) * mm});
            skLineSegment(sketch, "E169", {"start": v(0, 41) * mm, "end": v(81.07, 41) * mm, "construction": true});
            skLineSegment(sketch, "E170", {"start": v(0, 40) * mm, "end": v(10.33, 40) * mm, "construction": true});
            skSolve(sketch);
        }
        {
            var Q0;
            Q0 = qSketchRegion(id + "F11", true);
            var Q1;
            {var subQ4=sQuery(id+"F6.wireOp",EDGE,"E149.7");var subQ8=sQuery(id+"F6.wireOp",EDGE,"E149.3");var subQ10=sQuery(id+"F1.wireOp",EDGE,"E19.2.13");var subQ13=sQuery(id+"F1.wireOp",EDGE,"E42");var subQ16=makeQuery(id+"F7.opExtrude","SWEPT_FACE",FACE,{"disambiguationData":[OSD([subQ8,subQ4])]});Q1=makeQuery(id+"F9.boolean.opBoolean","MERGE",FACE,{"derivedFrom":[makeQuery(id+"F7.boolean.opBoolean","SPLIT",FACE,{"disambiguationData":[TD([makeQuery(id+"F2.opExtrude","SWEPT_FACE",FACE,{"disambiguationData":[OSD([subQ13])]})])],"derivedFrom":subQ16}),makeQuery(id+"F7.boolean.opBoolean","SPLIT",FACE,{"disambiguationData":[TD([makeQuery(id+"F2.opExtrude","SWEPT_FACE",FACE,{"disambiguationData":[OSD([subQ10])]})])],"derivedFrom":subQ16}),makeQuery(id+"F9.opExtrude","SWEPT_FACE",FACE,{"disambiguationData":[OSD([sQuery(id+"F8.wireOp",EDGE,"E154.0.15")])]})]});}
            extrude(context, id + "F12", {"entities" : qUnion([Q0]), "operationType" : NewBodyOperationType.ADD, "oppositeDirection" : true, "depth" : 179 * mm, "endBoundEntityFace" : qUnion([Q1]), "offsetDistance" : 25 * mm});
        }
        {
            var Q0;
            Q0=makeQuery(id+"F2.opExtrude","SWEPT_BODY",BODY,{"disambiguationData":[OSD([sQuery(id+"F1.wireOp",EDGE,"E19.1.1"),sQuery(id+"F1.wireOp",EDGE,"E19.2.9"),sQuery(id+"F1.wireOp",EDGE,"E19.2.13"),sQuery(id+"F1.wireOp",EDGE,"E19.3.0"),sQuery(id+"F1.wireOp",EDGE,"E26"),sQuery(id+"F1.wireOp",EDGE,"E27"),sQuery(id+"F1.wireOp",EDGE,"E31"),sQuery(id+"F1.wireOp",EDGE,"E32"),sQuery(id+"F1.wireOp",EDGE,"E34"),sQuery(id+"F1.wireOp",EDGE,"E35.trimOffspring"),sQuery(id+"F1.wireOp",EDGE,"E36.trimOffspring"),sQuery(id+"F1.wireOp",EDGE,"E39.0"),sQuery(id+"F1.wireOp",EDGE,"E39.0"),sQuery(id+"F1.wireOp",EDGE,"E41.0"),sQuery(id+"F1.wireOp",EDGE,"E42"),sQuery(id+"F1.wireOp",EDGE,"E45.0"),sQuery(id+"F1.wireOp",EDGE,"E46.trimOffspring"),sQuery(id+"F1.wireOp",EDGE,"E47.trimOffspring"),sQuery(id+"F1.wireOp",EDGE,"E48.trimOffspring"),sQuery(id+"F1.wireOp",EDGE,"E49.trimOffspring"),sQuery(id+"F1.wireOp",EDGE,"E52.0"),sQuery(id+"F1.wireOp",EDGE,"E53.0"),sQuery(id+"F1.wireOp",EDGE,"E55.trimOffspring"),sQuery(id+"F1.wireOp",EDGE,"E57"),sQuery(id+"F1.wireOp",EDGE,"E58"),sQuery(id+"F1.wireOp",EDGE,"E59.0"),sQuery(id+"F1.wireOp",EDGE,"E60"),sQuery(id+"F1.wireOp",EDGE,"E61"),sQuery(id+"F1.wireOp",EDGE,"E62.trimOffspring"),sQuery(id+"F1.wireOp",EDGE,"E63.trimOffspring"),sQuery(id+"F1.wireOp",EDGE,"E64.trimOffspring"),sQuery(id+"F1.wireOp",EDGE,"E65.0"),sQuery(id+"F1.wireOp",EDGE,"E66.0"),sQuery(id+"F1.wireOp",EDGE,"E66.1"),sQuery(id+"F1.wireOp",EDGE,"E67.0"),sQuery(id+"F1.wireOp",EDGE,"E68.0"),sQuery(id+"F1.wireOp",EDGE,"E69"),sQuery(id+"F1.wireOp",EDGE,"E70.0"),sQuery(id+"F1.wireOp",EDGE,"E72.0"),sQuery(id+"F1.wireOp",EDGE,"E73.0"),sQuery(id+"F1.wireOp",EDGE,"E75.trimOffspring"),sQuery(id+"F1.wireOp",EDGE,"E77.trimOffspring"),sQuery(id+"F1.wireOp",EDGE,"E78.0"),sQuery(id+"F1.wireOp",EDGE,"E79.trimOffspring"),sQuery(id+"F1.wireOp",EDGE,"E80.trimOffspring"),sQuery(id+"F1.wireOp",EDGE,"E81.0"),sQuery(id+"F1.wireOp",EDGE,"E82.trimOffspring"),sQuery(id+"F1.wireOp",EDGE,"E83.0"),sQuery(id+"F1.wireOp",EDGE,"E85.trimOffspring"),sQuery(id+"F1.wireOp",EDGE,"E87"),sQuery(id+"F1.wireOp",EDGE,"E89.trimOffspring"),sQuery(id+"F1.wireOp",EDGE,"E92.0"),sQuery(id+"F1.wireOp",EDGE,"E93.0"),sQuery(id+"F1.wireOp",EDGE,"E94"),sQuery(id+"F1.wireOp",EDGE,"E95.0"),sQuery(id+"F1.wireOp",EDGE,"E96.trimOffspring"),sQuery(id+"F1.wireOp",EDGE,"E97.trimOffspring"),sQuery(id+"F1.wireOp",EDGE,"E98"),sQuery(id+"F1.wireOp",EDGE,"E99"),sQuery(id+"F1.wireOp",EDGE,"E100.0"),sQuery(id+"F1.wireOp",EDGE,"E101.0"),sQuery(id+"F1.wireOp",EDGE,"E102.trimOffspring"),sQuery(id+"F1.wireOp",EDGE,"E103.0"),sQuery(id+"F1.wireOp",EDGE,"E104.0")])]});
            var Q1;
            Q1=makeQuery(id+"Fopt4IH3jrsNWrZ_1.boolean.opBoolean","MERGE",FACE,{"derivedFrom":[makeQuery(id+"F7.opExtrude","SWEPT_FACE",FACE,{"disambiguationData":[OSD([sQuery(id+"F6.wireOp",EDGE,"E149.9")])]}),makeQuery(id+"Fopt4IH3jrsNWrZ_1.opExtrude","SWEPT_FACE",FACE,{"disambiguationData":[OSD([sQuery(id+"F10.wireOp",EDGE,"E162.0")])]})]});
            mirror(context, id + "F13", {"operationType" : NewBodyOperationType.ADD, "entities" : qUnion([Q0]), "mirrorPlane" : qUnion([Q1])});
        }
    });
